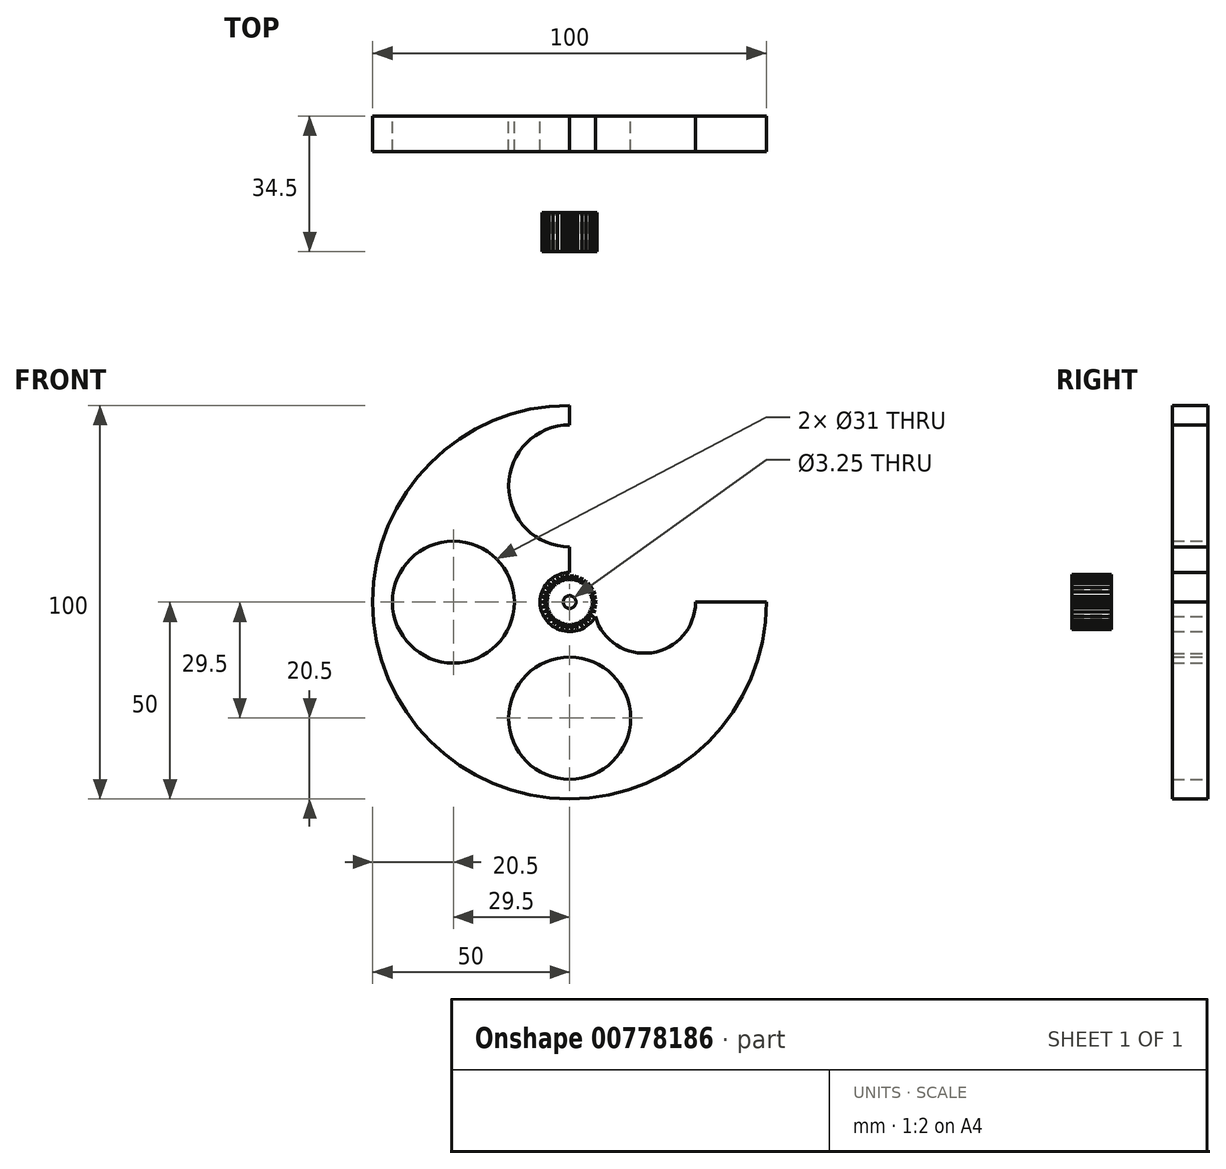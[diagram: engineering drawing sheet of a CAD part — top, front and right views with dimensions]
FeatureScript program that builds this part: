
annotation { "Feature Type Name" : "Feature", "Feature Type Description" : "" }
export const myFeature = defineFeature(function(context is Context, id is Id, definition is map)
    precondition{}
    {
        {
            var Q0;
            Q0=qCreatedBy(makeId("Front.planeOp"),FACE);
            var sketch = newSketch(context, id + "F0", { "sketchPlane" : qUnion([Q0])});
            skCircle(sketch, "E0", {"center": v(9.5, 0) * mm, "radius": 13 * mm});
            skCircle(sketch, "E1", {"center": v(-9.5, 0) * mm, "radius": 5.41 * mm});
            skCircle(sketch, "E2", {"center": v(9.5, 0) * mm, "radius": 11.5 * mm});
            skPoint(sketch, "E3", {"position": v(-4.3, 1.48) * mm});
            skPoint(sketch, "E4", {"position": v(-4.66, 2.41) * mm});
            skPoint(sketch, "E5", {"position": v(-5.18, 3.26) * mm});
            skPoint(sketch, "E6", {"position": v(-5.85, 4) * mm});
            skPoint(sketch, "E7", {"position": v(-6.65, 4.6) * mm});
            skPoint(sketch, "E8", {"position": v(-7.09, 4.85) * mm});
            skPoint(sketch, "E9", {"position": v(-7.55, 5.05) * mm});
            skPoint(sketch, "E10", {"position": v(-4.18, 1) * mm});
            skPoint(sketch, "E11", {"position": v(-4.45, 1.96) * mm});
            skPoint(sketch, "E12", {"position": v(-4.9, 2.85) * mm});
            skPoint(sketch, "E13", {"position": v(-5.5, 3.65) * mm});
            skPoint(sketch, "E14", {"position": v(-6.24, 4.32) * mm});
            skPoint(sketch, "E15", {"position": v(-4.11, 0.5) * mm});
            skLineSegment(sketch, "E16", {"start": v(-4.11, 0.5) * mm, "end": v(-2.62, 1.29) * mm});
            skLineSegment(sketch, "E17", {"start": v(-2.62, 1.29) * mm, "end": v(-4.3, 1.48) * mm});
            skLineSegment(sketch, "E18", {"start": v(-4.3, 1.48) * mm, "end": v(-2.97, 2.53) * mm});
            skLineSegment(sketch, "E19", {"start": v(-2.97, 2.53) * mm, "end": v(-4.66, 2.41) * mm});
            skLineSegment(sketch, "E20", {"start": v(-4.66, 2.41) * mm, "end": v(-3.55, 3.69) * mm});
            skLineSegment(sketch, "E21", {"start": v(-3.55, 3.69) * mm, "end": v(-5.18, 3.26) * mm});
            skLineSegment(sketch, "E22", {"start": v(-5.18, 3.26) * mm, "end": v(-4.33, 4.72) * mm});
            skLineSegment(sketch, "E23", {"start": v(-4.33, 4.72) * mm, "end": v(-5.85, 4) * mm});
            skLineSegment(sketch, "E24", {"start": v(-6.65, 4.6) * mm, "end": v(-5.28, 5.59) * mm});
            skLineSegment(sketch, "E25", {"start": v(-6.65, 4.6) * mm, "end": v(-6.38, 6.27) * mm});
            skPoint(sketch, "E26", {"position": v(-4.09, 0) * mm});
            skPoint(sketch, "E27", {"position": v(-4.11, -0.5) * mm});
            skPoint(sketch, "E28", {"position": v(-4.18, -1) * mm});
            skPoint(sketch, "E29", {"position": v(-4.3, -1.48) * mm});
            skPoint(sketch, "E30", {"position": v(-4.45, -1.96) * mm});
            skPoint(sketch, "E31", {"position": v(-4.66, -2.41) * mm});
            skPoint(sketch, "E32", {"position": v(-4.9, -2.85) * mm});
            skPoint(sketch, "E33", {"position": v(-5.18, -3.26) * mm});
            skPoint(sketch, "E34", {"position": v(-5.5, -3.65) * mm});
            skLineSegment(sketch, "E35", {"start": v(-4.11, 0.5) * mm, "end": v(-2.5, 0) * mm});
            skLineSegment(sketch, "E36", {"start": v(-2.5, 0) * mm, "end": v(-4.11, -0.5) * mm});
            skLineSegment(sketch, "E37", {"start": v(-4.11, -0.5) * mm, "end": v(-2.62, -1.29) * mm});
            skLineSegment(sketch, "E38", {"start": v(-4.3, -1.48) * mm, "end": v(-2.62, -1.29) * mm});
            skLineSegment(sketch, "E39", {"start": v(-4.3, -1.48) * mm, "end": v(-2.97, -2.53) * mm});
            skLineSegment(sketch, "E40", {"start": v(-2.97, -2.53) * mm, "end": v(-4.66, -2.41) * mm});
            skLineSegment(sketch, "E41", {"start": v(-4.66, -2.41) * mm, "end": v(-3.55, -3.69) * mm});
            skLineSegment(sketch, "E42", {"start": v(-3.55, -3.69) * mm, "end": v(-5.18, -3.26) * mm});
            skLineSegment(sketch, "E43", {"start": v(-5.18, -3.26) * mm, "end": v(-4.33, -4.72) * mm});
            skPoint(sketch, "E44", {"position": v(-8.5, 5.32) * mm});
            skPoint(sketch, "E45", {"position": v(-9, 5.39) * mm});
            skPoint(sketch, "E46", {"position": v(-9.5, 5.41) * mm});
            skPoint(sketch, "E47", {"position": v(-10, 5.39) * mm});
            skPoint(sketch, "E48", {"position": v(-10.98, 5.2) * mm});
            skPoint(sketch, "E49", {"position": v(-11.46, 5.05) * mm});
            skPoint(sketch, "E50", {"position": v(-11.91, 4.84) * mm});
            skPoint(sketch, "E51", {"position": v(-12.35, 4.6) * mm});
            skPoint(sketch, "E52", {"position": v(-12.76, 4.32) * mm});
            skPoint(sketch, "E53", {"position": v(-13.15, 4) * mm});
            skPoint(sketch, "E54", {"position": v(-13.5, 3.65) * mm});
            skPoint(sketch, "E55", {"position": v(-13.82, 3.26) * mm});
            skPoint(sketch, "E56", {"position": v(-8.02, 5.2) * mm});
            skPoint(sketch, "E57", {"position": v(-10.5, 5.32) * mm});
            skPoint(sketch, "E58", {"position": v(-14.1, 2.85) * mm});
            skPoint(sketch, "E59", {"position": v(-14.35, 2.41) * mm});
            skPoint(sketch, "E60", {"position": v(-14.55, 1.95) * mm});
            skPoint(sketch, "E61", {"position": v(-14.7, 1.48) * mm});
            skPoint(sketch, "E62", {"position": v(-14.82, 1) * mm});
            skPoint(sketch, "E63", {"position": v(-14.89, 0.5) * mm});
            skPoint(sketch, "E64", {"position": v(-14.91, 0) * mm});
            skPoint(sketch, "E65", {"position": v(-14.89, -0.5) * mm});
            skPoint(sketch, "E66", {"position": v(-14.82, -1) * mm});
            skPoint(sketch, "E67", {"position": v(-14.7, -1.48) * mm});
            skPoint(sketch, "E68", {"position": v(-14.55, -1.96) * mm});
            skPoint(sketch, "E69", {"position": v(-14.34, -2.41) * mm});
            skPoint(sketch, "E70", {"position": v(-14.1, -2.85) * mm});
            skPoint(sketch, "E71", {"position": v(-13.82, -3.26) * mm});
            skPoint(sketch, "E72", {"position": v(-13.5, -3.65) * mm});
            skPoint(sketch, "E73", {"position": v(-13.14, -4) * mm});
            skPoint(sketch, "E74", {"position": v(-12.76, -4.32) * mm});
            skPoint(sketch, "E75", {"position": v(-12.35, -4.6) * mm});
            skPoint(sketch, "E76", {"position": v(-11.9, -4.85) * mm});
            skPoint(sketch, "E77", {"position": v(-11.45, -5.05) * mm});
            skPoint(sketch, "E78", {"position": v(-10.98, -5.2) * mm});
            skPoint(sketch, "E79", {"position": v(-10.5, -5.32) * mm});
            skPoint(sketch, "E80", {"position": v(-10, -5.39) * mm});
            skPoint(sketch, "E81", {"position": v(-9.5, -5.41) * mm});
            skPoint(sketch, "E82", {"position": v(-9, -5.39) * mm});
            skPoint(sketch, "E83", {"position": v(-8.02, -5.2) * mm});
            skPoint(sketch, "E84", {"position": v(-7.54, -5.05) * mm});
            skPoint(sketch, "E85", {"position": v(-7.08, -4.84) * mm});
            skPoint(sketch, "E86", {"position": v(-6.65, -4.6) * mm});
            skPoint(sketch, "E87", {"position": v(-6.24, -4.32) * mm});
            skPoint(sketch, "E88", {"position": v(-5.85, -4) * mm});
            skPoint(sketch, "E89", {"position": v(-8.5, -5.32) * mm});
            skLineSegment(sketch, "E90", {"start": v(-7.55, 5.05) * mm, "end": v(-6.38, 6.27) * mm});
            skLineSegment(sketch, "E91", {"start": v(-5.28, 5.59) * mm, "end": v(-5.85, 4) * mm});
            skLineSegment(sketch, "E92", {"start": v(-7.55, 5.05) * mm, "end": v(-7.59, 6.73) * mm});
            skLineSegment(sketch, "E93", {"start": v(-7.59, 6.73) * mm, "end": v(-8.5, 5.32) * mm});
            skLineSegment(sketch, "E94", {"start": v(-8.5, 5.32) * mm, "end": v(-8.86, 6.97) * mm});
            skLineSegment(sketch, "E95", {"start": v(-8.86, 6.97) * mm, "end": v(-9.5, 5.41) * mm});
            skLineSegment(sketch, "E96", {"start": v(-10.15, 6.97) * mm, "end": v(-9.5, 5.41) * mm});
            skLineSegment(sketch, "E97", {"start": v(-10.5, 5.32) * mm, "end": v(-10.15, 6.97) * mm});
            skLineSegment(sketch, "E98", {"start": v(-11.42, 6.73) * mm, "end": v(-10.5, 5.32) * mm});
            skLineSegment(sketch, "E99", {"start": v(-11.46, 5.05) * mm, "end": v(-11.42, 6.73) * mm});
            skLineSegment(sketch, "E100", {"start": v(-11.46, 5.05) * mm, "end": v(-12.62, 6.26) * mm});
            skLineSegment(sketch, "E101", {"start": v(-12.35, 4.6) * mm, "end": v(-12.62, 6.26) * mm});
            skLineSegment(sketch, "E102", {"start": v(-12.35, 4.6) * mm, "end": v(-13.72, 5.58) * mm});
            skLineSegment(sketch, "E103", {"start": v(-13.15, 4) * mm, "end": v(-13.72, 5.58) * mm});
            skLineSegment(sketch, "E104", {"start": v(-13.5, 3.65) * mm, "end": v(-13.3, 3.47) * mm});
            skLineSegment(sketch, "E105", {"start": v(-14.67, 4.71) * mm, "end": v(-13.15, 4) * mm});
            skLineSegment(sketch, "E106", {"start": v(-13.82, 3.26) * mm, "end": v(-14.67, 4.71) * mm});
            skLineSegment(sketch, "E107", {"start": v(-15.45, 3.68) * mm, "end": v(-13.82, 3.26) * mm});
            skLineSegment(sketch, "E108", {"start": v(-15.45, 3.68) * mm, "end": v(-14.35, 2.41) * mm});
            skLineSegment(sketch, "E109", {"start": v(-16.03, 2.53) * mm, "end": v(-14.35, 2.41) * mm});
            skLineSegment(sketch, "E110", {"start": v(-16.03, 2.53) * mm, "end": v(-14.7, 1.48) * mm});
            skLineSegment(sketch, "E111", {"start": v(-16.37, 1.36) * mm, "end": v(-14.7, 1.48) * mm});
            skLineSegment(sketch, "E112", {"start": v(-16.37, 1.36) * mm, "end": v(-14.89, 0.5) * mm});
            skLineSegment(sketch, "E113", {"start": v(-16.5, 0) * mm, "end": v(-14.89, 0.5) * mm});
            skLineSegment(sketch, "E114", {"start": v(-16.5, 0) * mm, "end": v(-14.89, -0.5) * mm});
            skLineSegment(sketch, "E115", {"start": v(-16.38, -1.29) * mm, "end": v(-14.89, -0.5) * mm});
            skLineSegment(sketch, "E116", {"start": v(-16.38, -1.29) * mm, "end": v(-14.7, -1.48) * mm});
            skLineSegment(sketch, "E117", {"start": v(-16.03, -2.53) * mm, "end": v(-14.7, -1.48) * mm});
            skLineSegment(sketch, "E118", {"start": v(-16.03, -2.53) * mm, "end": v(-14.34, -2.41) * mm});
            skLineSegment(sketch, "E119", {"start": v(-15.45, -3.69) * mm, "end": v(-14.34, -2.41) * mm});
            skLineSegment(sketch, "E120", {"start": v(-15.45, -3.69) * mm, "end": v(-13.82, -3.26) * mm});
            skCircle(sketch, "E121", {"center": v(-9.5, 0) * mm, "radius": 7 * mm});
            skLineSegment(sketch, "E122", {"start": v(-14.67, -4.72) * mm, "end": v(-13.82, -3.26) * mm});
            skLineSegment(sketch, "E123", {"start": v(-14.67, -4.72) * mm, "end": v(-13.14, -4) * mm});
            skLineSegment(sketch, "E124", {"start": v(-13.55, -5.71) * mm, "end": v(-13.14, -4) * mm});
            skLineSegment(sketch, "E125", {"start": v(-13.55, -5.71) * mm, "end": v(-12.35, -4.6) * mm});
            skLineSegment(sketch, "E126", {"start": v(-12.62, -6.27) * mm, "end": v(-12.35, -4.6) * mm});
            skLineSegment(sketch, "E127", {"start": v(-12.62, -6.27) * mm, "end": v(-11.45, -5.05) * mm});
            skLineSegment(sketch, "E128", {"start": v(-11.41, -6.73) * mm, "end": v(-11.45, -5.05) * mm});
            skLineSegment(sketch, "E129", {"start": v(-11.41, -6.73) * mm, "end": v(-10.5, -5.32) * mm});
            skLineSegment(sketch, "E130", {"start": v(-10.14, -6.97) * mm, "end": v(-10.5, -5.32) * mm});
            skLineSegment(sketch, "E131", {"start": v(-10.14, -6.97) * mm, "end": v(-9.5, -5.41) * mm});
            skLineSegment(sketch, "E132", {"start": v(-8.86, -6.97) * mm, "end": v(-9.5, -5.41) * mm});
            skLineSegment(sketch, "E133", {"start": v(-8.86, -6.97) * mm, "end": v(-8.5, -5.32) * mm});
            skLineSegment(sketch, "E134", {"start": v(-7.58, -6.73) * mm, "end": v(-8.5, -5.32) * mm});
            skLineSegment(sketch, "E135", {"start": v(-7.58, -6.73) * mm, "end": v(-7.54, -5.05) * mm});
            skLineSegment(sketch, "E136", {"start": v(-6.32, -6.27) * mm, "end": v(-7.54, -5.05) * mm});
            skLineSegment(sketch, "E137", {"start": v(-6.32, -6.27) * mm, "end": v(-6.65, -4.6) * mm});
            skLineSegment(sketch, "E138", {"start": v(-5.1, -5.71) * mm, "end": v(-6.65, -4.6) * mm});
            skLineSegment(sketch, "E139", {"start": v(-5.1, -5.71) * mm, "end": v(-5.85, -4) * mm});
            skLineSegment(sketch, "E140", {"start": v(-5.85, -3.98) * mm, "end": v(-4.33, -4.72) * mm});
            skCircle(sketch, "E141", {"center": v(-9.5, 0) * mm, "radius": 7.5 * mm});
            skCircle(sketch, "E142", {"center": v(-9.5, 0) * mm, "radius": 50 * mm});
            skCircle(sketch, "E143", {"center": v(-9.5, 0) * mm, "radius": 6.5 * mm});
            skCircle(sketch, "E144", {"center": v(-9.5, 0) * mm, "radius": 1.63 * mm});
            skLineSegment(sketch, "E145", {"start": v(-9.5, 0) * mm, "end": v(-9.5, 50) * mm});
            skLineSegment(sketch, "E146", {"start": v(-9.5, 0) * mm, "end": v(-9.5, -50) * mm});
            skLineSegment(sketch, "E147", {"start": v(-9.5, 0) * mm, "end": v(-59.5, 0) * mm});
            skLineSegment(sketch, "E148", {"start": v(-9.5, 0) * mm, "end": v(40.5, 0) * mm});
            skPoint(sketch, "E149", {"position": v(-9.5, 45) * mm});
            skPoint(sketch, "E150", {"position": v(-54.5, 0) * mm});
            skPoint(sketch, "E151", {"position": v(35.5, 0) * mm});
            skPoint(sketch, "E152", {"position": v(-9.5, -45) * mm});
            skPoint(sketch, "E153", {"position": v(-39, 0) * mm});
            skCircle(sketch, "E154", {"center": v(-39, 0) * mm, "radius": 15.5 * mm});
            skPoint(sketch, "E155", {"position": v(-9.5, 29.5) * mm});
            skPoint(sketch, "E156", {"position": v(20, 0) * mm});
            skPoint(sketch, "E157", {"position": v(-9.5, -29.5) * mm});
            skCircle(sketch, "E158", {"center": v(-9.5, 29.5) * mm, "radius": 15.5 * mm});
            skCircle(sketch, "E159", {"center": v(20, 0) * mm, "radius": 15.5 * mm});
            skCircle(sketch, "E160", {"center": v(-9.5, -29.5) * mm, "radius": 15.5 * mm});
            skSolve(sketch);
        }
        {
            var Q0;
            {var subQ0=sQuery(id+"F0.wireOp",EDGE,"E145");var subQ5=sQuery(id+"F0.wireOp",EDGE,"E141");var subQ6=makeQuery(id+"F0.imprint","INTERSECT",VERTEX,{"derivedFrom":[subQ5,subQ0]});Q0=makeQuery(id+"F0.imprint","IMPRINT",FACE,{"disambiguationData":[TD([[makeQuery(id+"F0.imprint","IMPRINT",EDGE,{"disambiguationData":[TD([[subQ6,-1.0]])],"derivedFrom":subQ5}),-1.0]])]});}
            var Q1;
            {var subQ9=sQuery(id+"F0.wireOp",EDGE,"E0");var subQ11=sQuery(id+"F0.wireOp",EDGE,"E159");var subQ12=makeQuery(id+"F0.imprint","INTERSECT",VERTEX,{"disambiguationData":[OD(0.0)],"derivedFrom":[subQ9,subQ11]});Q1=makeQuery(id+"F0.imprint","IMPRINT",FACE,{"disambiguationData":[TD([[makeQuery(id+"F0.imprint","IMPRINT",EDGE,{"disambiguationData":[TD([[subQ12,-1.0]])],"derivedFrom":subQ9}),-1.0]])]});}
            var Q2;
            {var subQ1=sQuery(id+"F0.wireOp",EDGE,"E141");var subQ5=sQuery(id+"F0.wireOp",EDGE,"E0");var subQ6=makeQuery(id+"F0.imprint","INTERSECT",VERTEX,{"disambiguationData":[OD(1.0)],"derivedFrom":[subQ5,subQ1]});Q2=makeQuery(id+"F0.imprint","IMPRINT",FACE,{"disambiguationData":[TD([[makeQuery(id+"F0.imprint","IMPRINT",EDGE,{"disambiguationData":[TD([[subQ6,-1.0]])],"derivedFrom":subQ5}),-1.0]])]});}
            var Q3;
            {var subQ6=sQuery(id+"F0.wireOp",EDGE,"E147");var subQ9=sQuery(id+"F0.wireOp",EDGE,"E141");var subQ13=makeQuery(id+"F0.imprint","INTERSECT",VERTEX,{"derivedFrom":[subQ9,subQ6]});Q3=makeQuery(id+"F0.imprint","IMPRINT",FACE,{"disambiguationData":[TD([[makeQuery(id+"F0.imprint","IMPRINT",EDGE,{"disambiguationData":[TD([[subQ13,-1.0]])],"derivedFrom":subQ9}),-1.0]])]});}
            extrude(context, id + "F1", {"entities" : qUnion([Q0, Q1, Q2, Q3]), "endBound" : BoundingType.SYMMETRIC, "depth" : 9 * mm, "offsetDistance" : 25 * mm});
        }
        {
            var Q0;
            {var subQ0=sQuery(id+"F0.wireOp",EDGE,"E1");var subQ5=makeQuery(id+"F0.imprint","IMPRINT",VERTEX,{"derivedFrom":subQ0});Q0=makeQuery(id+"F0.imprint","IMPRINT",FACE,{"disambiguationData":[TD([[makeQuery(id+"F0.imprint","IMPRINT",EDGE,{"disambiguationData":[TD([[subQ5,1.0]])],"derivedFrom":subQ0}),1.0]])]});}
            var Q1;
            {var subQ2=sQuery(id+"F0.wireOp",EDGE,"E145");var subQ4=sQuery(id+"F0.wireOp",EDGE,"E144");var subQ5=makeQuery(id+"F0.imprint","INTERSECT",VERTEX,{"derivedFrom":[subQ4,subQ2]});Q1=makeQuery(id+"F0.imprint","IMPRINT",FACE,{"disambiguationData":[TD([[makeQuery(id+"F0.imprint","IMPRINT",EDGE,{"disambiguationData":[TD([[subQ5,1.0]])],"derivedFrom":subQ4}),-1.0]])]});}
            var Q2;
            {var subQ0=sQuery(id+"F0.wireOp",EDGE,"E147");var subQ1=sQuery(id+"F0.wireOp",EDGE,"E144");var subQ2=makeQuery(id+"F0.imprint","INTERSECT",VERTEX,{"derivedFrom":[subQ1,subQ0]});Q2=makeQuery(id+"F0.imprint","IMPRINT",FACE,{"disambiguationData":[TD([[makeQuery(id+"F0.imprint","IMPRINT",EDGE,{"disambiguationData":[TD([[subQ2,-1.0]])],"derivedFrom":subQ1}),-1.0]])]});}
            var Q3;
            {var subQ0=sQuery(id+"F0.wireOp",EDGE,"E1");var subQ10=makeQuery(id+"F0.imprint","INTERSECT",VERTEX,{"derivedFrom":[subQ0,sQuery(id+"F0.wireOp",EDGE,"E139")]});Q3=makeQuery(id+"F0.imprint","IMPRINT",FACE,{"disambiguationData":[TD([[makeQuery(id+"F0.imprint","IMPRINT",EDGE,{"disambiguationData":[TD([[subQ10,-1.0]])],"derivedFrom":subQ0}),1.0]])]});}
            var Q4;
            {var subQ0=sQuery(id+"F0.wireOp",EDGE,"E122");var subQ5=sQuery(id+"F0.wireOp",EDGE,"E143");var subQ6=makeQuery(id+"F0.imprint","INTERSECT",VERTEX,{"derivedFrom":[subQ0,subQ5]});Q4=makeQuery(id+"F0.imprint","IMPRINT",FACE,{"disambiguationData":[TD([[makeQuery(id+"F0.imprint","IMPRINT",EDGE,{"disambiguationData":[TD([[subQ6,-1.0]])],"derivedFrom":subQ5}),1.0]])]});}
            var Q5;
            {var subQ1=sQuery(id+"F0.wireOp",EDGE,"E122");var subQ3=sQuery(id+"F0.wireOp",EDGE,"E143");var subQ4=makeQuery(id+"F0.imprint","INTERSECT",VERTEX,{"derivedFrom":[subQ1,subQ3]});Q5=makeQuery(id+"F0.imprint","IMPRINT",FACE,{"disambiguationData":[TD([[makeQuery(id+"F0.imprint","IMPRINT",EDGE,{"disambiguationData":[TD([[subQ4,-1.0]])],"derivedFrom":subQ3}),-1.0]])]});}
            var Q6;
            {var subQ1=sQuery(id+"F0.wireOp",EDGE,"E119");var subQ3=sQuery(id+"F0.wireOp",EDGE,"E143");var subQ4=makeQuery(id+"F0.imprint","INTERSECT",VERTEX,{"derivedFrom":[subQ1,subQ3]});Q6=makeQuery(id+"F0.imprint","IMPRINT",FACE,{"disambiguationData":[TD([[makeQuery(id+"F0.imprint","IMPRINT",EDGE,{"disambiguationData":[TD([[subQ4,-1.0]])],"derivedFrom":subQ3}),-1.0]])]});}
            var Q7;
            {var subQ0=sQuery(id+"F0.wireOp",EDGE,"E119");var subQ5=sQuery(id+"F0.wireOp",EDGE,"E143");var subQ6=makeQuery(id+"F0.imprint","INTERSECT",VERTEX,{"derivedFrom":[subQ0,subQ5]});Q7=makeQuery(id+"F0.imprint","IMPRINT",FACE,{"disambiguationData":[TD([[makeQuery(id+"F0.imprint","IMPRINT",EDGE,{"disambiguationData":[TD([[subQ6,-1.0]])],"derivedFrom":subQ5}),1.0]])]});}
            var Q8;
            {var subQ1=sQuery(id+"F0.wireOp",EDGE,"E117");var subQ3=sQuery(id+"F0.wireOp",EDGE,"E143");var subQ4=makeQuery(id+"F0.imprint","INTERSECT",VERTEX,{"derivedFrom":[subQ1,subQ3]});Q8=makeQuery(id+"F0.imprint","IMPRINT",FACE,{"disambiguationData":[TD([[makeQuery(id+"F0.imprint","IMPRINT",EDGE,{"disambiguationData":[TD([[subQ4,-1.0]])],"derivedFrom":subQ3}),-1.0]])]});}
            var Q9;
            {var subQ0=sQuery(id+"F0.wireOp",EDGE,"E117");var subQ5=sQuery(id+"F0.wireOp",EDGE,"E143");var subQ6=makeQuery(id+"F0.imprint","INTERSECT",VERTEX,{"derivedFrom":[subQ0,subQ5]});Q9=makeQuery(id+"F0.imprint","IMPRINT",FACE,{"disambiguationData":[TD([[makeQuery(id+"F0.imprint","IMPRINT",EDGE,{"disambiguationData":[TD([[subQ6,-1.0]])],"derivedFrom":subQ5}),1.0]])]});}
            var Q10;
            {var subQ1=sQuery(id+"F0.wireOp",EDGE,"E115");var subQ3=sQuery(id+"F0.wireOp",EDGE,"E143");var subQ4=makeQuery(id+"F0.imprint","INTERSECT",VERTEX,{"derivedFrom":[subQ1,subQ3]});Q10=makeQuery(id+"F0.imprint","IMPRINT",FACE,{"disambiguationData":[TD([[makeQuery(id+"F0.imprint","IMPRINT",EDGE,{"disambiguationData":[TD([[subQ4,-1.0]])],"derivedFrom":subQ3}),-1.0]])]});}
            var Q11;
            {var subQ0=sQuery(id+"F0.wireOp",EDGE,"E115");var subQ5=sQuery(id+"F0.wireOp",EDGE,"E143");var subQ6=makeQuery(id+"F0.imprint","INTERSECT",VERTEX,{"derivedFrom":[subQ0,subQ5]});Q11=makeQuery(id+"F0.imprint","IMPRINT",FACE,{"disambiguationData":[TD([[makeQuery(id+"F0.imprint","IMPRINT",EDGE,{"disambiguationData":[TD([[subQ6,-1.0]])],"derivedFrom":subQ5}),1.0]])]});}
            var Q12;
            {var subQ0=sQuery(id+"F0.wireOp",EDGE,"E147");var subQ1=sQuery(id+"F0.wireOp",EDGE,"E113");var subQ2=makeQuery(id+"F0.imprint","INTERSECT",VERTEX,{"derivedFrom":[subQ1,subQ0]});Q12=makeQuery(id+"F0.imprint","IMPRINT",FACE,{"disambiguationData":[TD([[makeQuery(id+"F0.imprint","IMPRINT",EDGE,{"disambiguationData":[TD([[subQ2,-1.0]])],"derivedFrom":subQ1}),-1.0]])]});}
            var Q13;
            {var subQ0=sQuery(id+"F0.wireOp",EDGE,"E114");var subQ5=sQuery(id+"F0.wireOp",EDGE,"E143");var subQ6=makeQuery(id+"F0.imprint","INTERSECT",VERTEX,{"derivedFrom":[subQ0,subQ5]});Q13=makeQuery(id+"F0.imprint","IMPRINT",FACE,{"disambiguationData":[TD([[makeQuery(id+"F0.imprint","IMPRINT",EDGE,{"disambiguationData":[TD([[subQ6,1.0]])],"derivedFrom":subQ5}),-1.0]])]});}
            var Q14;
            {var subQ0=sQuery(id+"F0.wireOp",EDGE,"E114");var subQ5=sQuery(id+"F0.wireOp",EDGE,"E143");var subQ6=makeQuery(id+"F0.imprint","INTERSECT",VERTEX,{"derivedFrom":[subQ0,subQ5]});Q14=makeQuery(id+"F0.imprint","IMPRINT",FACE,{"disambiguationData":[TD([[makeQuery(id+"F0.imprint","IMPRINT",EDGE,{"disambiguationData":[TD([[subQ6,1.0]])],"derivedFrom":subQ5}),1.0]])]});}
            var Q15;
            {var subQ0=sQuery(id+"F0.wireOp",EDGE,"E113");var subQ5=sQuery(id+"F0.wireOp",EDGE,"E143");var subQ7=makeQuery(id+"F0.imprint","INTERSECT",VERTEX,{"derivedFrom":[subQ0,subQ5]});Q15=makeQuery(id+"F0.imprint","IMPRINT",FACE,{"disambiguationData":[TD([[makeQuery(id+"F0.imprint","IMPRINT",EDGE,{"disambiguationData":[TD([[subQ7,-1.0]])],"derivedFrom":subQ5}),1.0]])]});}
            var Q16;
            {var subQ0=sQuery(id+"F0.wireOp",EDGE,"E111");var subQ5=sQuery(id+"F0.wireOp",EDGE,"E143");var subQ7=makeQuery(id+"F0.imprint","INTERSECT",VERTEX,{"derivedFrom":[subQ0,subQ5]});Q16=makeQuery(id+"F0.imprint","IMPRINT",FACE,{"disambiguationData":[TD([[makeQuery(id+"F0.imprint","IMPRINT",EDGE,{"disambiguationData":[TD([[subQ7,-1.0]])],"derivedFrom":subQ5}),1.0]])]});}
            var Q17;
            {var subQ1=sQuery(id+"F0.wireOp",EDGE,"E111");var subQ3=sQuery(id+"F0.wireOp",EDGE,"E143");var subQ4=makeQuery(id+"F0.imprint","INTERSECT",VERTEX,{"derivedFrom":[subQ1,subQ3]});Q17=makeQuery(id+"F0.imprint","IMPRINT",FACE,{"disambiguationData":[TD([[makeQuery(id+"F0.imprint","IMPRINT",EDGE,{"disambiguationData":[TD([[subQ4,-1.0]])],"derivedFrom":subQ3}),-1.0]])]});}
            var Q18;
            {var subQ1=sQuery(id+"F0.wireOp",EDGE,"E109");var subQ3=sQuery(id+"F0.wireOp",EDGE,"E143");var subQ4=makeQuery(id+"F0.imprint","INTERSECT",VERTEX,{"derivedFrom":[subQ1,subQ3]});Q18=makeQuery(id+"F0.imprint","IMPRINT",FACE,{"disambiguationData":[TD([[makeQuery(id+"F0.imprint","IMPRINT",EDGE,{"disambiguationData":[TD([[subQ4,-1.0]])],"derivedFrom":subQ3}),-1.0]])]});}
            var Q19;
            {var subQ0=sQuery(id+"F0.wireOp",EDGE,"E109");var subQ5=sQuery(id+"F0.wireOp",EDGE,"E143");var subQ6=makeQuery(id+"F0.imprint","INTERSECT",VERTEX,{"derivedFrom":[subQ0,subQ5]});Q19=makeQuery(id+"F0.imprint","IMPRINT",FACE,{"disambiguationData":[TD([[makeQuery(id+"F0.imprint","IMPRINT",EDGE,{"disambiguationData":[TD([[subQ6,-1.0]])],"derivedFrom":subQ5}),1.0]])]});}
            var Q20;
            {var subQ1=sQuery(id+"F0.wireOp",EDGE,"E107");var subQ3=sQuery(id+"F0.wireOp",EDGE,"E143");var subQ4=makeQuery(id+"F0.imprint","INTERSECT",VERTEX,{"derivedFrom":[subQ1,subQ3]});Q20=makeQuery(id+"F0.imprint","IMPRINT",FACE,{"disambiguationData":[TD([[makeQuery(id+"F0.imprint","IMPRINT",EDGE,{"disambiguationData":[TD([[subQ4,-1.0]])],"derivedFrom":subQ3}),-1.0]])]});}
            var Q21;
            {var subQ0=sQuery(id+"F0.wireOp",EDGE,"E107");var subQ5=sQuery(id+"F0.wireOp",EDGE,"E143");var subQ6=makeQuery(id+"F0.imprint","INTERSECT",VERTEX,{"derivedFrom":[subQ0,subQ5]});Q21=makeQuery(id+"F0.imprint","IMPRINT",FACE,{"disambiguationData":[TD([[makeQuery(id+"F0.imprint","IMPRINT",EDGE,{"disambiguationData":[TD([[subQ6,-1.0]])],"derivedFrom":subQ5}),1.0]])]});}
            var Q22;
            {var subQ1=sQuery(id+"F0.wireOp",EDGE,"E105");var subQ3=sQuery(id+"F0.wireOp",EDGE,"E143");var subQ4=makeQuery(id+"F0.imprint","INTERSECT",VERTEX,{"derivedFrom":[subQ1,subQ3]});Q22=makeQuery(id+"F0.imprint","IMPRINT",FACE,{"disambiguationData":[TD([[makeQuery(id+"F0.imprint","IMPRINT",EDGE,{"disambiguationData":[TD([[subQ4,-1.0]])],"derivedFrom":subQ3}),-1.0]])]});}
            var Q23;
            {var subQ1=sQuery(id+"F0.wireOp",EDGE,"E1");var subQ5=makeQuery(id+"F0.imprint","IMPRINT",VERTEX,{"derivedFrom":subQ1});Q23=makeQuery(id+"F0.imprint","IMPRINT",FACE,{"disambiguationData":[TD([[makeQuery(id+"F0.imprint","IMPRINT",EDGE,{"disambiguationData":[TD([[subQ5,1.0]])],"derivedFrom":subQ1}),-1.0]])]});}
            var Q24;
            {var subQ1=sQuery(id+"F0.wireOp",EDGE,"E124");var subQ3=sQuery(id+"F0.wireOp",EDGE,"E143");var subQ4=makeQuery(id+"F0.imprint","INTERSECT",VERTEX,{"derivedFrom":[subQ1,subQ3]});Q24=makeQuery(id+"F0.imprint","IMPRINT",FACE,{"disambiguationData":[TD([[makeQuery(id+"F0.imprint","IMPRINT",EDGE,{"disambiguationData":[TD([[subQ4,-1.0]])],"derivedFrom":subQ3}),-1.0]])]});}
            var Q25;
            {var subQ0=sQuery(id+"F0.wireOp",EDGE,"E124");var subQ5=sQuery(id+"F0.wireOp",EDGE,"E143");var subQ7=makeQuery(id+"F0.imprint","INTERSECT",VERTEX,{"derivedFrom":[subQ0,subQ5]});Q25=makeQuery(id+"F0.imprint","IMPRINT",FACE,{"disambiguationData":[TD([[makeQuery(id+"F0.imprint","IMPRINT",EDGE,{"disambiguationData":[TD([[subQ7,-1.0]])],"derivedFrom":subQ5}),1.0]])]});}
            var Q26;
            {var subQ1=sQuery(id+"F0.wireOp",EDGE,"E126");var subQ3=sQuery(id+"F0.wireOp",EDGE,"E143");var subQ4=makeQuery(id+"F0.imprint","INTERSECT",VERTEX,{"derivedFrom":[subQ1,subQ3]});Q26=makeQuery(id+"F0.imprint","IMPRINT",FACE,{"disambiguationData":[TD([[makeQuery(id+"F0.imprint","IMPRINT",EDGE,{"disambiguationData":[TD([[subQ4,-1.0]])],"derivedFrom":subQ3}),-1.0]])]});}
            var Q27;
            {var subQ0=sQuery(id+"F0.wireOp",EDGE,"E126");var subQ5=sQuery(id+"F0.wireOp",EDGE,"E143");var subQ6=makeQuery(id+"F0.imprint","INTERSECT",VERTEX,{"derivedFrom":[subQ0,subQ5]});Q27=makeQuery(id+"F0.imprint","IMPRINT",FACE,{"disambiguationData":[TD([[makeQuery(id+"F0.imprint","IMPRINT",EDGE,{"disambiguationData":[TD([[subQ6,-1.0]])],"derivedFrom":subQ5}),1.0]])]});}
            var Q28;
            {var subQ1=sQuery(id+"F0.wireOp",EDGE,"E128");var subQ3=sQuery(id+"F0.wireOp",EDGE,"E143");var subQ4=makeQuery(id+"F0.imprint","INTERSECT",VERTEX,{"derivedFrom":[subQ1,subQ3]});Q28=makeQuery(id+"F0.imprint","IMPRINT",FACE,{"disambiguationData":[TD([[makeQuery(id+"F0.imprint","IMPRINT",EDGE,{"disambiguationData":[TD([[subQ4,-1.0]])],"derivedFrom":subQ3}),-1.0]])]});}
            var Q29;
            {var subQ0=sQuery(id+"F0.wireOp",EDGE,"E128");var subQ5=sQuery(id+"F0.wireOp",EDGE,"E143");var subQ6=makeQuery(id+"F0.imprint","INTERSECT",VERTEX,{"derivedFrom":[subQ0,subQ5]});Q29=makeQuery(id+"F0.imprint","IMPRINT",FACE,{"disambiguationData":[TD([[makeQuery(id+"F0.imprint","IMPRINT",EDGE,{"disambiguationData":[TD([[subQ6,-1.0]])],"derivedFrom":subQ5}),1.0]])]});}
            var Q30;
            {var subQ1=sQuery(id+"F0.wireOp",EDGE,"E130");var subQ3=sQuery(id+"F0.wireOp",EDGE,"E143");var subQ4=makeQuery(id+"F0.imprint","INTERSECT",VERTEX,{"derivedFrom":[subQ1,subQ3]});Q30=makeQuery(id+"F0.imprint","IMPRINT",FACE,{"disambiguationData":[TD([[makeQuery(id+"F0.imprint","IMPRINT",EDGE,{"disambiguationData":[TD([[subQ4,-1.0]])],"derivedFrom":subQ3}),-1.0]])]});}
            var Q31;
            {var subQ0=sQuery(id+"F0.wireOp",EDGE,"E143");var subQ3=sQuery(id+"F0.wireOp",EDGE,"E131");var subQ4=makeQuery(id+"F0.imprint","INTERSECT",VERTEX,{"derivedFrom":[subQ3,subQ0]});Q31=makeQuery(id+"F0.imprint","IMPRINT",FACE,{"disambiguationData":[TD([[makeQuery(id+"F0.imprint","IMPRINT",EDGE,{"disambiguationData":[TD([[subQ4,-1.0]])],"derivedFrom":subQ3}),1.0]])]});}
            var Q32;
            {var subQ1=sQuery(id+"F0.wireOp",EDGE,"E132");var subQ3=sQuery(id+"F0.wireOp",EDGE,"E143");var subQ4=makeQuery(id+"F0.imprint","INTERSECT",VERTEX,{"derivedFrom":[subQ1,subQ3]});Q32=makeQuery(id+"F0.imprint","IMPRINT",FACE,{"disambiguationData":[TD([[makeQuery(id+"F0.imprint","IMPRINT",EDGE,{"disambiguationData":[TD([[subQ4,-1.0]])],"derivedFrom":subQ3}),-1.0]])]});}
            var Q33;
            {var subQ0=sQuery(id+"F0.wireOp",EDGE,"E132");var subQ5=sQuery(id+"F0.wireOp",EDGE,"E143");var subQ6=makeQuery(id+"F0.imprint","INTERSECT",VERTEX,{"derivedFrom":[subQ0,subQ5]});Q33=makeQuery(id+"F0.imprint","IMPRINT",FACE,{"disambiguationData":[TD([[makeQuery(id+"F0.imprint","IMPRINT",EDGE,{"disambiguationData":[TD([[subQ6,-1.0]])],"derivedFrom":subQ5}),1.0]])]});}
            var Q34;
            {var subQ1=sQuery(id+"F0.wireOp",EDGE,"E134");var subQ3=sQuery(id+"F0.wireOp",EDGE,"E143");var subQ4=makeQuery(id+"F0.imprint","INTERSECT",VERTEX,{"derivedFrom":[subQ1,subQ3]});Q34=makeQuery(id+"F0.imprint","IMPRINT",FACE,{"disambiguationData":[TD([[makeQuery(id+"F0.imprint","IMPRINT",EDGE,{"disambiguationData":[TD([[subQ4,-1.0]])],"derivedFrom":subQ3}),-1.0]])]});}
            var Q35;
            {var subQ0=sQuery(id+"F0.wireOp",EDGE,"E134");var subQ5=sQuery(id+"F0.wireOp",EDGE,"E143");var subQ7=makeQuery(id+"F0.imprint","INTERSECT",VERTEX,{"derivedFrom":[subQ0,subQ5]});Q35=makeQuery(id+"F0.imprint","IMPRINT",FACE,{"disambiguationData":[TD([[makeQuery(id+"F0.imprint","IMPRINT",EDGE,{"disambiguationData":[TD([[subQ7,-1.0]])],"derivedFrom":subQ5}),1.0]])]});}
            var Q36;
            {var subQ0=sQuery(id+"F0.wireOp",EDGE,"E136");var subQ1=sQuery(id+"F0.wireOp",EDGE,"E121");var subQ2=makeQuery(id+"F0.imprint","INTERSECT",VERTEX,{"derivedFrom":[subQ1,subQ0]});Q36=makeQuery(id+"F0.imprint","IMPRINT",FACE,{"disambiguationData":[TD([[makeQuery(id+"F0.imprint","IMPRINT",EDGE,{"disambiguationData":[TD([[subQ2,-1.0]])],"derivedFrom":subQ1}),1.0]])]});}
            var Q37;
            {var subQ0=sQuery(id+"F0.wireOp",EDGE,"E136");var subQ5=sQuery(id+"F0.wireOp",EDGE,"E143");var subQ7=makeQuery(id+"F0.imprint","INTERSECT",VERTEX,{"derivedFrom":[subQ0,subQ5]});Q37=makeQuery(id+"F0.imprint","IMPRINT",FACE,{"disambiguationData":[TD([[makeQuery(id+"F0.imprint","IMPRINT",EDGE,{"disambiguationData":[TD([[subQ7,-1.0]])],"derivedFrom":subQ5}),1.0]])]});}
            var Q38;
            {var subQ0=sQuery(id+"F0.wireOp",EDGE,"E138");var subQ1=sQuery(id+"F0.wireOp",EDGE,"E121");var subQ2=makeQuery(id+"F0.imprint","INTERSECT",VERTEX,{"derivedFrom":[subQ1,subQ0]});Q38=makeQuery(id+"F0.imprint","IMPRINT",FACE,{"disambiguationData":[TD([[makeQuery(id+"F0.imprint","IMPRINT",EDGE,{"disambiguationData":[TD([[subQ2,-1.0]])],"derivedFrom":subQ1}),1.0]])]});}
            var Q39;
            {var subQ1=sQuery(id+"F0.wireOp",EDGE,"E1");var subQ3=sQuery(id+"F0.wireOp",EDGE,"E139");var subQ4=makeQuery(id+"F0.imprint","INTERSECT",VERTEX,{"derivedFrom":[subQ1,subQ3]});Q39=makeQuery(id+"F0.imprint","IMPRINT",FACE,{"disambiguationData":[TD([[makeQuery(id+"F0.imprint","IMPRINT",EDGE,{"disambiguationData":[TD([[subQ4,1.0]])],"derivedFrom":subQ3}),1.0]])]});}
            var Q40;
            {var subQ1=sQuery(id+"F0.wireOp",EDGE,"E43");var subQ3=sQuery(id+"F0.wireOp",EDGE,"E143");var subQ4=makeQuery(id+"F0.imprint","INTERSECT",VERTEX,{"derivedFrom":[subQ1,subQ3]});Q40=makeQuery(id+"F0.imprint","IMPRINT",FACE,{"disambiguationData":[TD([[makeQuery(id+"F0.imprint","IMPRINT",EDGE,{"disambiguationData":[TD([[subQ4,1.0]])],"derivedFrom":subQ3}),-1.0]])]});}
            var Q41;
            {var subQ1=sQuery(id+"F0.wireOp",EDGE,"E1");var subQ3=sQuery(id+"F0.wireOp",EDGE,"E140");var subQ4=makeQuery(id+"F0.imprint","INTERSECT",VERTEX,{"derivedFrom":[subQ1,subQ3]});Q41=makeQuery(id+"F0.imprint","IMPRINT",FACE,{"disambiguationData":[TD([[makeQuery(id+"F0.imprint","IMPRINT",EDGE,{"disambiguationData":[TD([[subQ4,-1.0]])],"derivedFrom":subQ3}),1.0]])]});}
            var Q42;
            {var subQ1=sQuery(id+"F0.wireOp",EDGE,"E41");var subQ3=sQuery(id+"F0.wireOp",EDGE,"E143");var subQ4=makeQuery(id+"F0.imprint","INTERSECT",VERTEX,{"derivedFrom":[subQ1,subQ3]});Q42=makeQuery(id+"F0.imprint","IMPRINT",FACE,{"disambiguationData":[TD([[makeQuery(id+"F0.imprint","IMPRINT",EDGE,{"disambiguationData":[TD([[subQ4,1.0]])],"derivedFrom":subQ3}),-1.0]])]});}
            var Q43;
            {var subQ0=sQuery(id+"F0.wireOp",EDGE,"E41");var subQ5=sQuery(id+"F0.wireOp",EDGE,"E143");var subQ6=makeQuery(id+"F0.imprint","INTERSECT",VERTEX,{"derivedFrom":[subQ0,subQ5]});Q43=makeQuery(id+"F0.imprint","IMPRINT",FACE,{"disambiguationData":[TD([[makeQuery(id+"F0.imprint","IMPRINT",EDGE,{"disambiguationData":[TD([[subQ6,1.0]])],"derivedFrom":subQ5}),1.0]])]});}
            var Q44;
            {var subQ0=sQuery(id+"F0.wireOp",EDGE,"E39");var subQ1=sQuery(id+"F0.wireOp",EDGE,"E0");var subQ2=makeQuery(id+"F0.imprint","INTERSECT",VERTEX,{"derivedFrom":[subQ1,subQ0]});Q44=makeQuery(id+"F0.imprint","IMPRINT",FACE,{"disambiguationData":[TD([[makeQuery(id+"F0.imprint","IMPRINT",EDGE,{"disambiguationData":[TD([[subQ2,-1.0]])],"derivedFrom":subQ1}),-1.0]])]});}
            var Q45;
            {var subQ0=sQuery(id+"F0.wireOp",EDGE,"E39");var subQ5=sQuery(id+"F0.wireOp",EDGE,"E143");var subQ6=makeQuery(id+"F0.imprint","INTERSECT",VERTEX,{"derivedFrom":[subQ0,subQ5]});Q45=makeQuery(id+"F0.imprint","IMPRINT",FACE,{"disambiguationData":[TD([[makeQuery(id+"F0.imprint","IMPRINT",EDGE,{"disambiguationData":[TD([[subQ6,1.0]])],"derivedFrom":subQ5}),1.0]])]});}
            var Q46;
            {var subQ0=sQuery(id+"F0.wireOp",EDGE,"E39");var subQ1=sQuery(id+"F0.wireOp",EDGE,"E0");var subQ2=makeQuery(id+"F0.imprint","INTERSECT",VERTEX,{"derivedFrom":[subQ1,subQ0]});Q46=makeQuery(id+"F0.imprint","IMPRINT",FACE,{"disambiguationData":[TD([[makeQuery(id+"F0.imprint","IMPRINT",EDGE,{"disambiguationData":[TD([[subQ2,-1.0]])],"derivedFrom":subQ1}),1.0]])]});}
            var Q47;
            {var subQ1=sQuery(id+"F0.wireOp",EDGE,"E37");var subQ3=sQuery(id+"F0.wireOp",EDGE,"E143");var subQ4=makeQuery(id+"F0.imprint","INTERSECT",VERTEX,{"derivedFrom":[subQ1,subQ3]});Q47=makeQuery(id+"F0.imprint","IMPRINT",FACE,{"disambiguationData":[TD([[makeQuery(id+"F0.imprint","IMPRINT",EDGE,{"disambiguationData":[TD([[subQ4,1.0]])],"derivedFrom":subQ3}),-1.0]])]});}
            var Q48;
            {var subQ0=sQuery(id+"F0.wireOp",EDGE,"E37");var subQ1=sQuery(id+"F0.wireOp",EDGE,"E0");var subQ2=makeQuery(id+"F0.imprint","INTERSECT",VERTEX,{"derivedFrom":[subQ1,subQ0]});Q48=makeQuery(id+"F0.imprint","IMPRINT",FACE,{"disambiguationData":[TD([[makeQuery(id+"F0.imprint","IMPRINT",EDGE,{"disambiguationData":[TD([[subQ2,-1.0]])],"derivedFrom":subQ1}),-1.0]])]});}
            var Q49;
            {var subQ1=sQuery(id+"F0.wireOp",EDGE,"E35");var subQ3=sQuery(id+"F0.wireOp",EDGE,"E143");var subQ4=makeQuery(id+"F0.imprint","INTERSECT",VERTEX,{"derivedFrom":[subQ1,subQ3]});Q49=makeQuery(id+"F0.imprint","IMPRINT",FACE,{"disambiguationData":[TD([[makeQuery(id+"F0.imprint","IMPRINT",EDGE,{"disambiguationData":[TD([[subQ4,1.0]])],"derivedFrom":subQ3}),-1.0]])]});}
            var Q50;
            {var subQ0=sQuery(id+"F0.wireOp",EDGE,"E37");var subQ1=sQuery(id+"F0.wireOp",EDGE,"E0");var subQ2=makeQuery(id+"F0.imprint","INTERSECT",VERTEX,{"derivedFrom":[subQ1,subQ0]});Q50=makeQuery(id+"F0.imprint","IMPRINT",FACE,{"disambiguationData":[TD([[makeQuery(id+"F0.imprint","IMPRINT",EDGE,{"disambiguationData":[TD([[subQ2,-1.0]])],"derivedFrom":subQ1}),1.0]])]});}
            var Q51;
            {var subQ1=sQuery(id+"F0.wireOp",EDGE,"E36");var subQ3=sQuery(id+"F0.wireOp",EDGE,"E143");var subQ4=makeQuery(id+"F0.imprint","INTERSECT",VERTEX,{"derivedFrom":[subQ1,subQ3]});Q51=makeQuery(id+"F0.imprint","IMPRINT",FACE,{"disambiguationData":[TD([[makeQuery(id+"F0.imprint","IMPRINT",EDGE,{"disambiguationData":[TD([[subQ4,-1.0]])],"derivedFrom":subQ3}),-1.0]])]});}
            var Q52;
            {var subQ0=sQuery(id+"F0.wireOp",EDGE,"E148");var subQ1=sQuery(id+"F0.wireOp",EDGE,"E0");var subQ2=makeQuery(id+"F0.imprint","INTERSECT",VERTEX,{"disambiguationData":[OD(1.0)],"derivedFrom":[subQ1,subQ0]});Q52=makeQuery(id+"F0.imprint","IMPRINT",FACE,{"disambiguationData":[TD([[makeQuery(id+"F0.imprint","IMPRINT",EDGE,{"disambiguationData":[TD([[subQ2,-1.0]])],"derivedFrom":subQ1}),1.0]])]});}
            var Q53;
            {var subQ0=sQuery(id+"F0.wireOp",EDGE,"E35");var subQ1=sQuery(id+"F0.wireOp",EDGE,"E0");var subQ2=makeQuery(id+"F0.imprint","INTERSECT",VERTEX,{"derivedFrom":[subQ1,subQ0]});Q53=makeQuery(id+"F0.imprint","IMPRINT",FACE,{"disambiguationData":[TD([[makeQuery(id+"F0.imprint","IMPRINT",EDGE,{"disambiguationData":[TD([[subQ2,-1.0]])],"derivedFrom":subQ1}),1.0]])]});}
            var Q54;
            {var subQ0=sQuery(id+"F0.wireOp",EDGE,"E35");var subQ1=sQuery(id+"F0.wireOp",EDGE,"E0");var subQ2=makeQuery(id+"F0.imprint","INTERSECT",VERTEX,{"derivedFrom":[subQ1,subQ0]});Q54=makeQuery(id+"F0.imprint","IMPRINT",FACE,{"disambiguationData":[TD([[makeQuery(id+"F0.imprint","IMPRINT",EDGE,{"disambiguationData":[TD([[subQ2,-1.0]])],"derivedFrom":subQ1}),-1.0]])]});}
            var Q55;
            {var subQ0=sQuery(id+"F0.wireOp",EDGE,"E148");var subQ1=sQuery(id+"F0.wireOp",EDGE,"E0");var subQ2=makeQuery(id+"F0.imprint","INTERSECT",VERTEX,{"disambiguationData":[OD(1.0)],"derivedFrom":[subQ1,subQ0]});Q55=makeQuery(id+"F0.imprint","IMPRINT",FACE,{"disambiguationData":[TD([[makeQuery(id+"F0.imprint","IMPRINT",EDGE,{"disambiguationData":[TD([[subQ2,-1.0]])],"derivedFrom":subQ1}),-1.0]])]});}
            var Q56;
            {var subQ1=sQuery(id+"F0.wireOp",EDGE,"E16");var subQ3=sQuery(id+"F0.wireOp",EDGE,"E143");var subQ4=makeQuery(id+"F0.imprint","INTERSECT",VERTEX,{"derivedFrom":[subQ1,subQ3]});Q56=makeQuery(id+"F0.imprint","IMPRINT",FACE,{"disambiguationData":[TD([[makeQuery(id+"F0.imprint","IMPRINT",EDGE,{"disambiguationData":[TD([[subQ4,-1.0]])],"derivedFrom":subQ3}),-1.0]])]});}
            var Q57;
            {var subQ0=sQuery(id+"F0.wireOp",EDGE,"E17");var subQ1=sQuery(id+"F0.wireOp",EDGE,"E0");var subQ2=makeQuery(id+"F0.imprint","INTERSECT",VERTEX,{"derivedFrom":[subQ1,subQ0]});Q57=makeQuery(id+"F0.imprint","IMPRINT",FACE,{"disambiguationData":[TD([[makeQuery(id+"F0.imprint","IMPRINT",EDGE,{"disambiguationData":[TD([[subQ2,-1.0]])],"derivedFrom":subQ1}),1.0]])]});}
            var Q58;
            {var subQ0=sQuery(id+"F0.wireOp",EDGE,"E19");var subQ1=sQuery(id+"F0.wireOp",EDGE,"E0");var subQ2=makeQuery(id+"F0.imprint","INTERSECT",VERTEX,{"derivedFrom":[subQ1,subQ0]});Q58=makeQuery(id+"F0.imprint","IMPRINT",FACE,{"disambiguationData":[TD([[makeQuery(id+"F0.imprint","IMPRINT",EDGE,{"disambiguationData":[TD([[subQ2,-1.0]])],"derivedFrom":subQ1}),-1.0]])]});}
            var Q59;
            {var subQ0=sQuery(id+"F0.wireOp",EDGE,"E18");var subQ5=sQuery(id+"F0.wireOp",EDGE,"E143");var subQ6=makeQuery(id+"F0.imprint","INTERSECT",VERTEX,{"derivedFrom":[subQ0,subQ5]});Q59=makeQuery(id+"F0.imprint","IMPRINT",FACE,{"disambiguationData":[TD([[makeQuery(id+"F0.imprint","IMPRINT",EDGE,{"disambiguationData":[TD([[subQ6,-1.0]])],"derivedFrom":subQ5}),1.0]])]});}
            var Q60;
            {var subQ0=sQuery(id+"F0.wireOp",EDGE,"E17");var subQ1=sQuery(id+"F0.wireOp",EDGE,"E0");var subQ2=makeQuery(id+"F0.imprint","INTERSECT",VERTEX,{"derivedFrom":[subQ1,subQ0]});Q60=makeQuery(id+"F0.imprint","IMPRINT",FACE,{"disambiguationData":[TD([[makeQuery(id+"F0.imprint","IMPRINT",EDGE,{"disambiguationData":[TD([[subQ2,-1.0]])],"derivedFrom":subQ1}),-1.0]])]});}
            var Q61;
            {var subQ0=sQuery(id+"F0.wireOp",EDGE,"E19");var subQ1=sQuery(id+"F0.wireOp",EDGE,"E0");var subQ2=makeQuery(id+"F0.imprint","INTERSECT",VERTEX,{"derivedFrom":[subQ1,subQ0]});Q61=makeQuery(id+"F0.imprint","IMPRINT",FACE,{"disambiguationData":[TD([[makeQuery(id+"F0.imprint","IMPRINT",EDGE,{"disambiguationData":[TD([[subQ2,-1.0]])],"derivedFrom":subQ1}),1.0]])]});}
            var Q62;
            {var subQ1=sQuery(id+"F0.wireOp",EDGE,"E20");var subQ3=sQuery(id+"F0.wireOp",EDGE,"E143");var subQ4=makeQuery(id+"F0.imprint","INTERSECT",VERTEX,{"derivedFrom":[subQ1,subQ3]});Q62=makeQuery(id+"F0.imprint","IMPRINT",FACE,{"disambiguationData":[TD([[makeQuery(id+"F0.imprint","IMPRINT",EDGE,{"disambiguationData":[TD([[subQ4,-1.0]])],"derivedFrom":subQ3}),-1.0]])]});}
            var Q63;
            {var subQ0=sQuery(id+"F0.wireOp",EDGE,"E20");var subQ5=sQuery(id+"F0.wireOp",EDGE,"E143");var subQ6=makeQuery(id+"F0.imprint","INTERSECT",VERTEX,{"derivedFrom":[subQ0,subQ5]});Q63=makeQuery(id+"F0.imprint","IMPRINT",FACE,{"disambiguationData":[TD([[makeQuery(id+"F0.imprint","IMPRINT",EDGE,{"disambiguationData":[TD([[subQ6,-1.0]])],"derivedFrom":subQ5}),1.0]])]});}
            var Q64;
            {var subQ1=sQuery(id+"F0.wireOp",EDGE,"E22");var subQ3=sQuery(id+"F0.wireOp",EDGE,"E143");var subQ4=makeQuery(id+"F0.imprint","INTERSECT",VERTEX,{"derivedFrom":[subQ1,subQ3]});Q64=makeQuery(id+"F0.imprint","IMPRINT",FACE,{"disambiguationData":[TD([[makeQuery(id+"F0.imprint","IMPRINT",EDGE,{"disambiguationData":[TD([[subQ4,-1.0]])],"derivedFrom":subQ3}),-1.0]])]});}
            var Q65;
            {var subQ0=sQuery(id+"F0.wireOp",EDGE,"E22");var subQ5=sQuery(id+"F0.wireOp",EDGE,"E143");var subQ6=makeQuery(id+"F0.imprint","INTERSECT",VERTEX,{"derivedFrom":[subQ0,subQ5]});Q65=makeQuery(id+"F0.imprint","IMPRINT",FACE,{"disambiguationData":[TD([[makeQuery(id+"F0.imprint","IMPRINT",EDGE,{"disambiguationData":[TD([[subQ6,-1.0]])],"derivedFrom":subQ5}),1.0]])]});}
            var Q66;
            {var subQ1=sQuery(id+"F0.wireOp",EDGE,"E24");var subQ3=sQuery(id+"F0.wireOp",EDGE,"E143");var subQ4=makeQuery(id+"F0.imprint","INTERSECT",VERTEX,{"derivedFrom":[subQ1,subQ3]});Q66=makeQuery(id+"F0.imprint","IMPRINT",FACE,{"disambiguationData":[TD([[makeQuery(id+"F0.imprint","IMPRINT",EDGE,{"disambiguationData":[TD([[subQ4,1.0]])],"derivedFrom":subQ3}),-1.0]])]});}
            var Q67;
            {var subQ3=sQuery(id+"F0.wireOp",EDGE,"E24");var subQ5=sQuery(id+"F0.wireOp",EDGE,"E143");var subQ7=makeQuery(id+"F0.imprint","INTERSECT",VERTEX,{"derivedFrom":[subQ3,subQ5]});Q67=makeQuery(id+"F0.imprint","IMPRINT",FACE,{"disambiguationData":[TD([[makeQuery(id+"F0.imprint","IMPRINT",EDGE,{"disambiguationData":[TD([[subQ7,1.0]])],"derivedFrom":subQ5}),1.0]])]});}
            var Q68;
            {var subQ1=sQuery(id+"F0.wireOp",EDGE,"E25");var subQ3=sQuery(id+"F0.wireOp",EDGE,"E143");var subQ4=makeQuery(id+"F0.imprint","INTERSECT",VERTEX,{"derivedFrom":[subQ1,subQ3]});Q68=makeQuery(id+"F0.imprint","IMPRINT",FACE,{"disambiguationData":[TD([[makeQuery(id+"F0.imprint","IMPRINT",EDGE,{"disambiguationData":[TD([[subQ4,-1.0]])],"derivedFrom":subQ3}),-1.0]])]});}
            var Q69;
            {var subQ0=sQuery(id+"F0.wireOp",EDGE,"E25");var subQ5=sQuery(id+"F0.wireOp",EDGE,"E143");var subQ6=makeQuery(id+"F0.imprint","INTERSECT",VERTEX,{"derivedFrom":[subQ0,subQ5]});Q69=makeQuery(id+"F0.imprint","IMPRINT",FACE,{"disambiguationData":[TD([[makeQuery(id+"F0.imprint","IMPRINT",EDGE,{"disambiguationData":[TD([[subQ6,-1.0]])],"derivedFrom":subQ5}),1.0]])]});}
            var Q70;
            {var subQ1=sQuery(id+"F0.wireOp",EDGE,"E92");var subQ3=sQuery(id+"F0.wireOp",EDGE,"E143");var subQ4=makeQuery(id+"F0.imprint","INTERSECT",VERTEX,{"derivedFrom":[subQ1,subQ3]});Q70=makeQuery(id+"F0.imprint","IMPRINT",FACE,{"disambiguationData":[TD([[makeQuery(id+"F0.imprint","IMPRINT",EDGE,{"disambiguationData":[TD([[subQ4,-1.0]])],"derivedFrom":subQ3}),-1.0]])]});}
            var Q71;
            {var subQ0=sQuery(id+"F0.wireOp",EDGE,"E92");var subQ5=sQuery(id+"F0.wireOp",EDGE,"E143");var subQ6=makeQuery(id+"F0.imprint","INTERSECT",VERTEX,{"derivedFrom":[subQ0,subQ5]});Q71=makeQuery(id+"F0.imprint","IMPRINT",FACE,{"disambiguationData":[TD([[makeQuery(id+"F0.imprint","IMPRINT",EDGE,{"disambiguationData":[TD([[subQ6,-1.0]])],"derivedFrom":subQ5}),1.0]])]});}
            var Q72;
            {var subQ1=sQuery(id+"F0.wireOp",EDGE,"E94");var subQ3=sQuery(id+"F0.wireOp",EDGE,"E143");var subQ4=makeQuery(id+"F0.imprint","INTERSECT",VERTEX,{"derivedFrom":[subQ1,subQ3]});Q72=makeQuery(id+"F0.imprint","IMPRINT",FACE,{"disambiguationData":[TD([[makeQuery(id+"F0.imprint","IMPRINT",EDGE,{"disambiguationData":[TD([[subQ4,-1.0]])],"derivedFrom":subQ3}),-1.0]])]});}
            var Q73;
            {var subQ3=sQuery(id+"F0.wireOp",EDGE,"E143");var subQ7=sQuery(id+"F0.wireOp",EDGE,"E95");var subQ9=makeQuery(id+"F0.imprint","INTERSECT",VERTEX,{"derivedFrom":[subQ7,subQ3]});Q73=makeQuery(id+"F0.imprint","IMPRINT",FACE,{"disambiguationData":[TD([[makeQuery(id+"F0.imprint","IMPRINT",EDGE,{"disambiguationData":[TD([[subQ9,-1.0]])],"derivedFrom":subQ7}),1.0]])]});}
            var Q74;
            {var subQ1=sQuery(id+"F0.wireOp",EDGE,"E96");var subQ3=sQuery(id+"F0.wireOp",EDGE,"E143");var subQ4=makeQuery(id+"F0.imprint","INTERSECT",VERTEX,{"derivedFrom":[subQ1,subQ3]});Q74=makeQuery(id+"F0.imprint","IMPRINT",FACE,{"disambiguationData":[TD([[makeQuery(id+"F0.imprint","IMPRINT",EDGE,{"disambiguationData":[TD([[subQ4,-1.0]])],"derivedFrom":subQ3}),-1.0]])]});}
            var Q75;
            {var subQ0=sQuery(id+"F0.wireOp",EDGE,"E96");var subQ5=sQuery(id+"F0.wireOp",EDGE,"E143");var subQ6=makeQuery(id+"F0.imprint","INTERSECT",VERTEX,{"derivedFrom":[subQ0,subQ5]});Q75=makeQuery(id+"F0.imprint","IMPRINT",FACE,{"disambiguationData":[TD([[makeQuery(id+"F0.imprint","IMPRINT",EDGE,{"disambiguationData":[TD([[subQ6,-1.0]])],"derivedFrom":subQ5}),1.0]])]});}
            var Q76;
            {var subQ0=sQuery(id+"F0.wireOp",EDGE,"E121");var subQ1=sQuery(id+"F0.wireOp",EDGE,"E98");var subQ2=makeQuery(id+"F0.imprint","INTERSECT",VERTEX,{"derivedFrom":[subQ1,subQ0]});Q76=makeQuery(id+"F0.imprint","IMPRINT",FACE,{"disambiguationData":[TD([[makeQuery(id+"F0.imprint","IMPRINT",EDGE,{"disambiguationData":[TD([[subQ2,-1.0]])],"derivedFrom":subQ1}),-1.0]])]});}
            var Q77;
            {var subQ0=sQuery(id+"F0.wireOp",EDGE,"E98");var subQ5=sQuery(id+"F0.wireOp",EDGE,"E143");var subQ6=makeQuery(id+"F0.imprint","INTERSECT",VERTEX,{"derivedFrom":[subQ0,subQ5]});Q77=makeQuery(id+"F0.imprint","IMPRINT",FACE,{"disambiguationData":[TD([[makeQuery(id+"F0.imprint","IMPRINT",EDGE,{"disambiguationData":[TD([[subQ6,-1.0]])],"derivedFrom":subQ5}),1.0]])]});}
            var Q78;
            {var subQ1=sQuery(id+"F0.wireOp",EDGE,"E100");var subQ3=sQuery(id+"F0.wireOp",EDGE,"E143");var subQ4=makeQuery(id+"F0.imprint","INTERSECT",VERTEX,{"derivedFrom":[subQ1,subQ3]});Q78=makeQuery(id+"F0.imprint","IMPRINT",FACE,{"disambiguationData":[TD([[makeQuery(id+"F0.imprint","IMPRINT",EDGE,{"disambiguationData":[TD([[subQ4,-1.0]])],"derivedFrom":subQ3}),-1.0]])]});}
            var Q79;
            {var subQ0=sQuery(id+"F0.wireOp",EDGE,"E100");var subQ5=sQuery(id+"F0.wireOp",EDGE,"E143");var subQ7=makeQuery(id+"F0.imprint","INTERSECT",VERTEX,{"derivedFrom":[subQ0,subQ5]});Q79=makeQuery(id+"F0.imprint","IMPRINT",FACE,{"disambiguationData":[TD([[makeQuery(id+"F0.imprint","IMPRINT",EDGE,{"disambiguationData":[TD([[subQ7,-1.0]])],"derivedFrom":subQ5}),1.0]])]});}
            var Q80;
            {var subQ1=sQuery(id+"F0.wireOp",EDGE,"E102");var subQ3=sQuery(id+"F0.wireOp",EDGE,"E143");var subQ4=makeQuery(id+"F0.imprint","INTERSECT",VERTEX,{"derivedFrom":[subQ1,subQ3]});Q80=makeQuery(id+"F0.imprint","IMPRINT",FACE,{"disambiguationData":[TD([[makeQuery(id+"F0.imprint","IMPRINT",EDGE,{"disambiguationData":[TD([[subQ4,-1.0]])],"derivedFrom":subQ3}),-1.0]])]});}
            var Q81;
            {var subQ0=sQuery(id+"F0.wireOp",EDGE,"E102");var subQ5=sQuery(id+"F0.wireOp",EDGE,"E143");var subQ6=makeQuery(id+"F0.imprint","INTERSECT",VERTEX,{"derivedFrom":[subQ0,subQ5]});Q81=makeQuery(id+"F0.imprint","IMPRINT",FACE,{"disambiguationData":[TD([[makeQuery(id+"F0.imprint","IMPRINT",EDGE,{"disambiguationData":[TD([[subQ6,-1.0]])],"derivedFrom":subQ5}),1.0]])]});}
            extrude(context, id + "F2", {"entities" : qUnion([Q0, Q1, Q2, Q3, Q4, Q5, Q6, Q7, Q8, Q9, Q10, Q11, Q12, Q13, Q14, Q15, Q16, Q17, Q18, Q19, Q20, Q21, Q22, Q23, Q24, Q25, Q26, Q27, Q28, Q29, Q30, Q31, Q32, Q33, Q34, Q35, Q36, Q37, Q38, Q39, Q40, Q41, Q42, Q43, Q44, Q45, Q46, Q47, Q48, Q49, Q50, Q51, Q52, Q53, Q54, Q55, Q56, Q57, Q58, Q59, Q60, Q61, Q62, Q63, Q64, Q65, Q66, Q67, Q68, Q69, Q70, Q71, Q72, Q73, Q74, Q75, Q76, Q77, Q78, Q79, Q80, Q81]), "depth" : 30 * mm, "offsetDistance" : 25 * mm, "hasSecondDirection" : true, "secondDirectionOppositeDirection" : false, "secondDirectionDepth" : 20 * mm});
        }
    });
